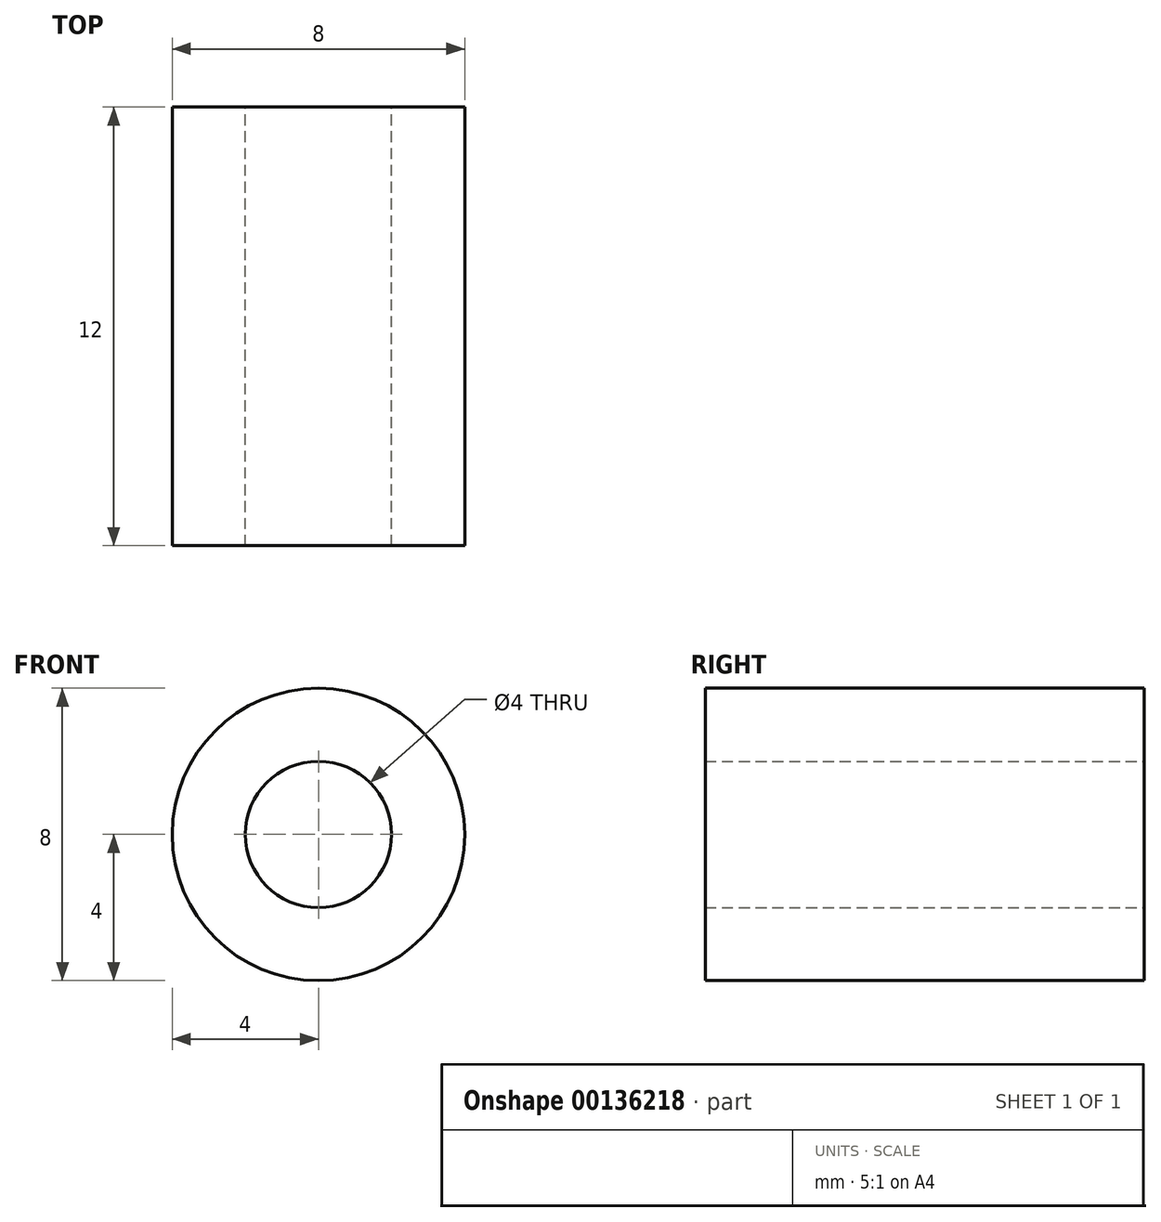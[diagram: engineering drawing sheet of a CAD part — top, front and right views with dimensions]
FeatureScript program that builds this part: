
annotation { "Feature Type Name" : "Feature", "Feature Type Description" : "" }
export const myFeature = defineFeature(function(context is Context, id is Id, definition is map)
    precondition{}
    {
        {
            var Q0;
            Q0=qCreatedBy(makeId("Front.planeOp"),FACE);
            var sketch = newSketch(context, id + "F0", { "sketchPlane" : qUnion([Q0])});
            skCircle(sketch, "E0", {"center": v(0, 0) * mm, "radius": 4 * mm});
            skCircle(sketch, "E1", {"center": v(0, 0) * mm, "radius": 2 * mm});
            skSolve(sketch);
        }
        {
            var Q0;
            Q0 = qSketchRegion(id + "F0", true);
            extrude(context, id + "F1", {"entities" : qUnion([Q0]), "depth" : 12 * mm});
        }
    });
